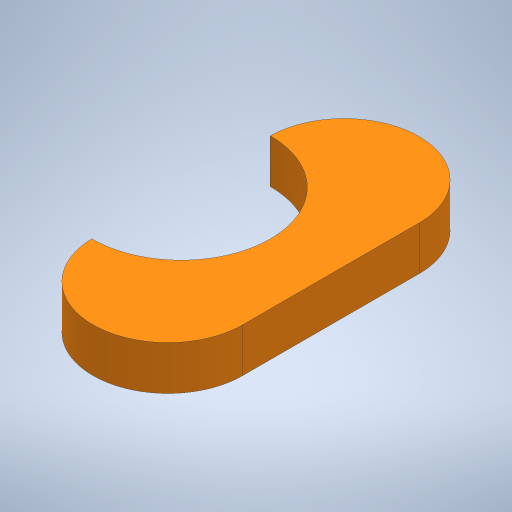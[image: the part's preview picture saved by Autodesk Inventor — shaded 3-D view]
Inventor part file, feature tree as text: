
AUTODESK INVENTOR PART (.ipt)
format: ipt  version: 2023 (Build 270158000, 158)  size: 231,936 bytes
history: native  units: mm
features: extrude x2, sketch x2
ambient origin geometry x8: Origin, YZ Plane, XZ Plane, XY Plane, X Axis, Y Axis, Z Axis, Center Point
bodies: Solid1 (feature_tree)
feature tree (4):
  extrude  "Extrusion1"  Depth=13.6mm
  extrude  "Extrusion2"  Depth=4.0mm
  sketch  "Sketch1"  dims[d0=16.0mm d1=13.6mm]
  sketch  "Sketch2"  dims[d3=4.0mm d4=0.0mm d5=16.2mm d6=0.0mm d7=0.0mm]
